# Revit family: Control_Panels-Lutron-LV16
name_source: partatom
category: Electrical Equipment
revit_build: Autodesk Revit 2017 (Build: 20160225_1515(x64)
units: mm (PartAtom-declared; Revit-internal decimal feet)

## family parameters
Cut with Voids When Loaded = No
Host = Face
OmniClass Number = 23.80.30.11.17
OmniClass Title = Distribution Boards and Control Panels
Panel Configuration = Two Columns, Circuits Across
Part Type = Panelboard
Room Calculation Point = No
Round Connector Dimension = Use Radius
Shared = No

## types (2) — shared parameters
Constraints = 1
Description = Low-Voltage Enclosure
Finish = Steel - Lutron - Black
Frequency = 50 Hz
Ground Bus = No
Instruction Sheet Link = http://www.lutron.com
Load Classification = Other
MCB Rating = 1 A
Manufacturer = Lutron Electronics Co., Inc
Manufacturer Fax Number = 610-282-1243
Neutral Bus = No
Neutral Rating = 0.00%
Number of Poles = 1
Overall Depth = 4.29 "
Overall Height = 16.09 "
Overall Width = 18.09 "
Performance URL = http://www.lutron.com
Phase = 1
Power Factor = 1
Product Documentation Link = http://www.lutron.com
Product Name = Lighting Control Panels
Product Page URL = http://www.lutron.com
Series = myRoom
SubFeed Lugs = No
URL = http://www.lutron.com
Unit Weight = 0.00 lb
Version = 2017 - v1.0a
Video Link = https://www.youtube.com
Warranty URL = http://www.lutron.com
zero-valued in all types: Cost, Default Elevation

## per-type parameters (varying)
| type | Electrical Potential | Feed Through Control Circuit Voltage | Voltage |
| LV16-120 | 120 V | 120 V | 120 V~ 50/60 Hz 2 A |
| LV16-230 | 220 V | 220 V | 220 –240 V~ 50/60 Hz 2 A |

note: column(s) folded — value = type name in every type: Model

## geometry (parser evidence)
native form markers: Sweep x2
no freeform markers — native parametric forms only
